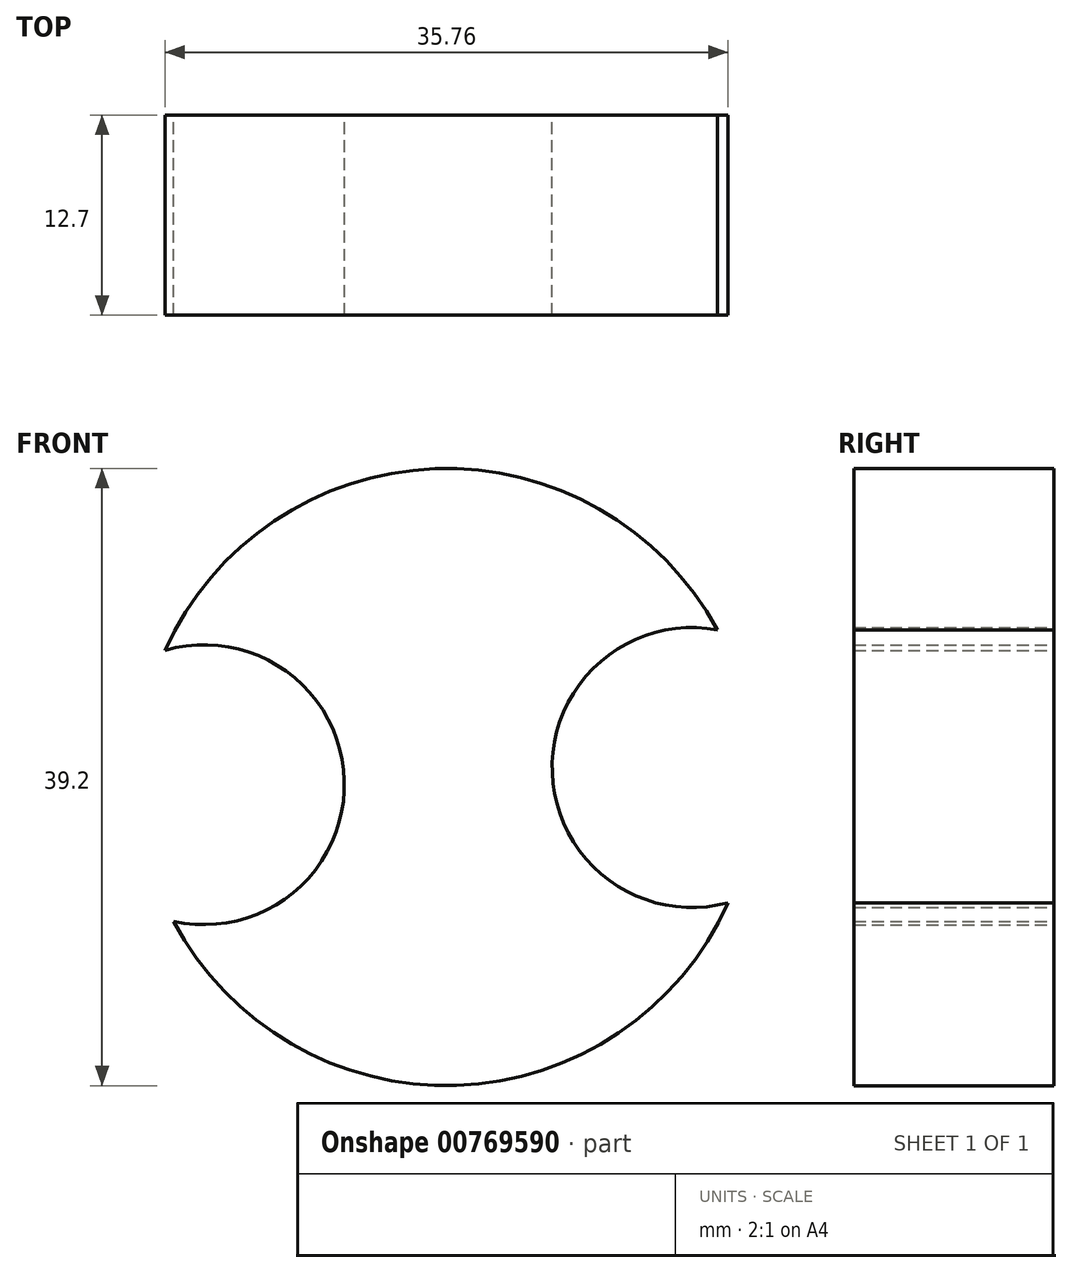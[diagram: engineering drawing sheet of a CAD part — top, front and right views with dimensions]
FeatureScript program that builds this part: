
annotation { "Feature Type Name" : "Feature", "Feature Type Description" : "" }
export const myFeature = defineFeature(function(context is Context, id is Id, definition is map)
    precondition{}
    {
        {
            var Q0;
            Q0=qCreatedBy(makeId("Front.planeOp"),FACE);
            var sketch = newSketch(context, id + "F0", { "sketchPlane" : qUnion([Q0])});
            skCircle(sketch, "E0", {"center": v(-22.81, -3.53) * mm, "radius": 19.6 * mm});
            skSolve(sketch);
        }
        {
            var Q0;
            Q0 = qSketchRegion(id + "F0", true);
            extrude(context, id + "F1", {"entities" : qUnion([Q0]), "depth" : 12.7 * mm, "offsetDistance" : 25.4 * mm});
        }
        {
            var Q0;
            Q0=qCreatedBy(makeId("Front.planeOp"),FACE);
            var sketch = newSketch(context, id + "F2", { "sketchPlane" : qUnion([Q0])});
            skPoint(sketch, "E1", {"position": v(-38.18, -4.01) * mm});
            skPoint(sketch, "E2", {"position": v(-7.2, -2.92) * mm});
            skPoint(sketch, "E3", {"position": v(-23.66, -2.92) * mm});
            skSolve(sketch);
        }
        {
            var Q0;
            Q0=sQuery(id+"F2.wireOp",VERTEX,"E1");
            var Q1;
            Q1=sQuery(id+"F2.wireOp",VERTEX,"E2");
            var Q2;
            Q2=makeQuery(id+"F1.opExtrude","SWEPT_BODY",BODY,{"disambiguationData":[OSD([sQuery(id+"F0.wireOp",EDGE,"E0")])]});
            hole(context, id + "F3", {"style" : HoleStyle.SIMPLE, "endStyle" : HoleEndStyle.THROUGH, "oppositeDirection" : true, "holeDiameter" : 17.78 * mm, "majorDiameter" : 6.35 * mm, "isTappedThrough" : true, "tappedDepth" : 12.7 * mm, "tapClearance" : 3, "locations" : qUnion([Q0, Q1]), "scope" : qUnion([Q2])});
        }
    });
